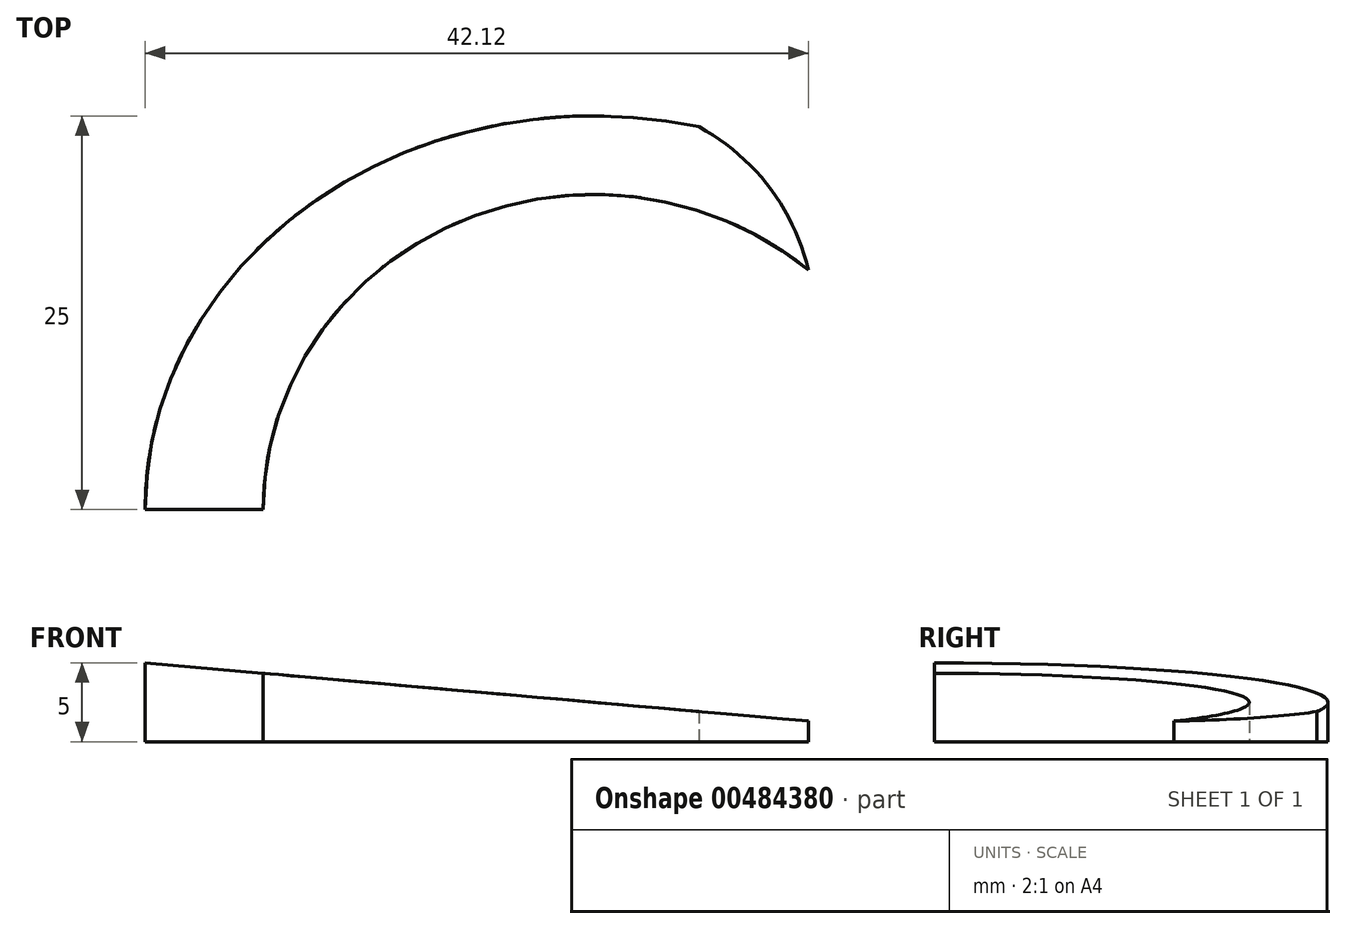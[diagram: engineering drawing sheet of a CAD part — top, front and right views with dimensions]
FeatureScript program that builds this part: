
annotation { "Feature Type Name" : "Feature", "Feature Type Description" : "" }
export const myFeature = defineFeature(function(context is Context, id is Id, definition is map)
    precondition{}
    {
        {
            var Q0;
            Q0=qCreatedBy(makeId("Top.planeOp"),FACE);
            var sketch = newSketch(context, id + "F0", { "sketchPlane" : qUnion([Q0])});
            skEllipse(sketch, "E0", {"center": v(0, 0) * mm, "majorRadius": 28.5 * mm, "minorRadius": 25 * mm, "majorAxis": v(1, 0)});
            skEllipse(sketch, "E1", {"center": v(0, 0) * mm, "majorRadius": 21 * mm, "minorRadius": 20 * mm, "majorAxis": v(-1, 0)});
            skLineSegment(sketch, "E2", {"start": v(-28.5, 0) * mm, "end": v(-21, 0) * mm});
            skLineSegment(sketch, "E3", {"start": v(27.5, 0) * mm, "end": v(19.9, 6.37) * mm});
            skLineSegment(sketch, "E4", {"start": v(21, 0) * mm, "end": v(28.5, 0) * mm});
            skCircle(sketch, "E5", {"center": v(0, 0) * mm, "radius": 7.5 * mm});
            skEllipse(sketch, "E6", {"center": v(0, 0) * mm, "majorRadius": 28.5 * mm, "minorRadius": 30 * mm, "majorAxis": v(1, 0)});
            skEllipse(sketch, "E7", {"center": v(0, 0) * mm, "majorRadius": 24 * mm, "minorRadius": 24 * mm, "majorAxis": v(-1, 0)});
            skArc(sketch, "E8", {"start": v(13.62, 15.22) * mm, "mid": v(11.12, 20.5) * mm, "end": v(6.68, 24.3) * mm});
            skSolve(sketch);
        }
        {
            var Q0;
            Q0=qCreatedBy(makeId("Front.planeOp"),FACE);
            var sketch = newSketch(context, id + "F1", { "sketchPlane" : qUnion([Q0])});
            skLineSegment(sketch, "E9", {"start": v(28.5, 0) * mm, "end": v(-28.5, 0) * mm});
            skLineSegment(sketch, "E10", {"start": v(-28.5, 0) * mm, "end": v(-28.5, 5) * mm});
            skLineSegment(sketch, "E11", {"start": v(-28.5, 5) * mm, "end": v(28.5, 0) * mm});
            skSolve(sketch);
        }
        {
            var Q0;
            {var subQ0=sQuery(id+"F0.wireOp",EDGE,"E2");var subQ1=sQuery(id+"F0.wireOp",EDGE,"E1");var subQ2=makeQuery(id+"F0.imprint","INTERSECT",VERTEX,{"derivedFrom":[subQ1,subQ0]});Q0=makeQuery(id+"F0.imprint","IMPRINT",FACE,{"disambiguationData":[TD([[makeQuery(id+"F0.imprint","IMPRINT",EDGE,{"disambiguationData":[TD([[subQ2,1.0]])],"derivedFrom":subQ1}),-1.0]])]});}
            var Q1;
            {var subQ0=sQuery(id+"F0.wireOp",EDGE,"E2");var subQ5=sQuery(id+"F0.wireOp",EDGE,"E7");var subQ6=makeQuery(id+"F0.imprint","INTERSECT",VERTEX,{"derivedFrom":[subQ0,subQ5]});Q1=makeQuery(id+"F0.imprint","IMPRINT",FACE,{"disambiguationData":[TD([[makeQuery(id+"F0.imprint","IMPRINT",EDGE,{"disambiguationData":[TD([[subQ6,1.0]])],"derivedFrom":subQ5}),-1.0]])]});}
            extrude(context, id + "F2", {"entities" : qUnion([Q0, Q1]), "depth" : 5 * mm, "offsetDistance" : 25 * mm});
        }
        {
            var Q0;
            Q0 = qSketchRegion(id + "F1", true);
            extrude(context, id + "F3", {"entities" : qUnion([Q0]), "operationType" : NewBodyOperationType.INTERSECT, "oppositeDirection" : true, "depth" : 40 * mm, "offsetDistance" : 25 * mm});
        }
    });
